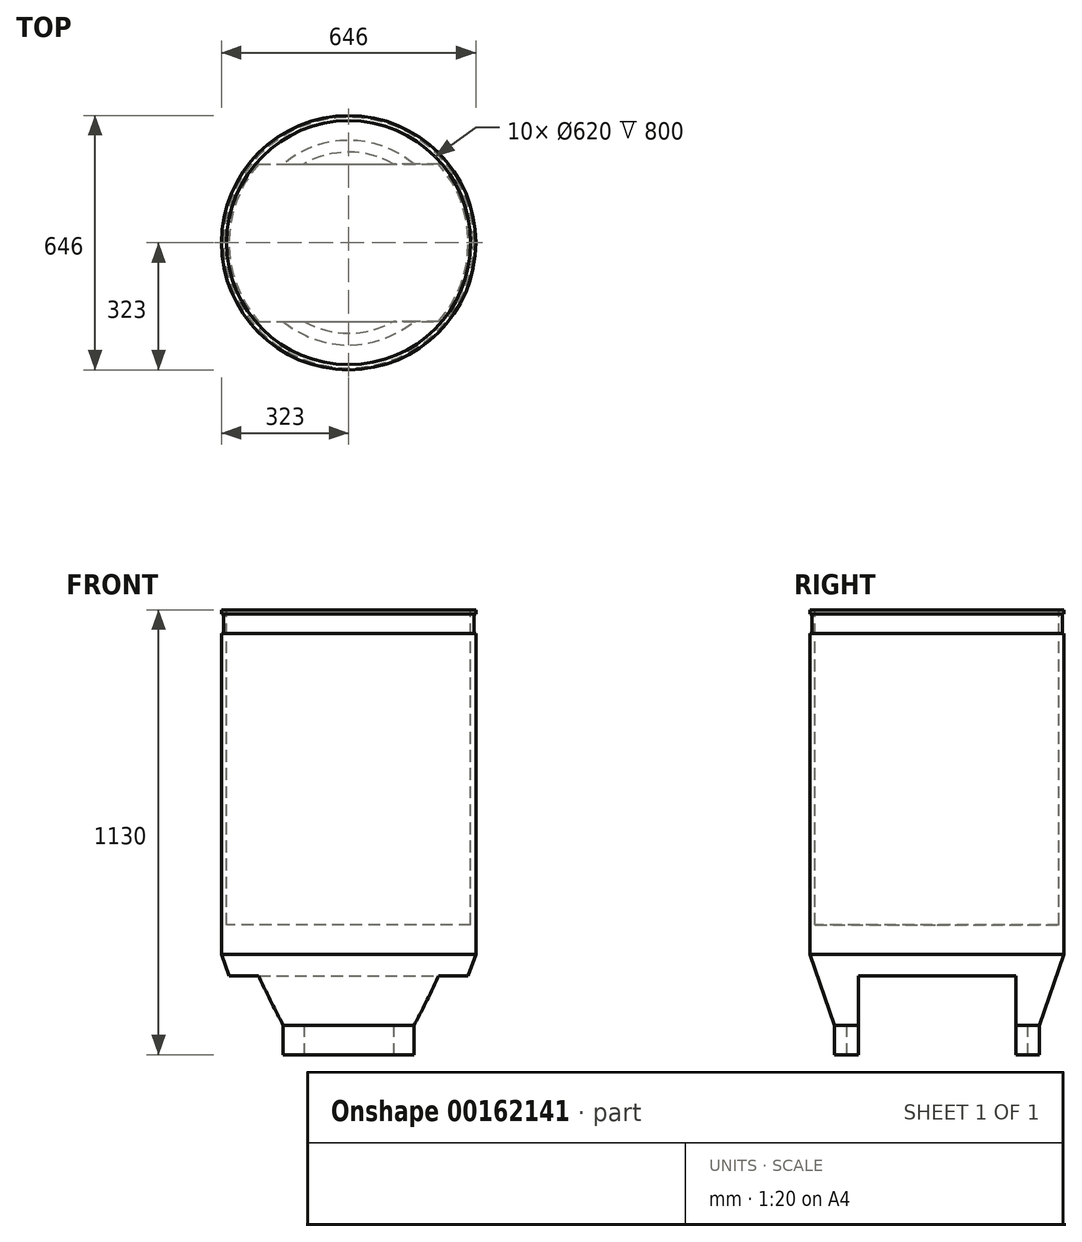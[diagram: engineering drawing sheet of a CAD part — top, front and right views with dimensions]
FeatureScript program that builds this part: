
annotation { "Feature Type Name" : "Feature", "Feature Type Description" : "" }
export const myFeature = defineFeature(function(context is Context, id is Id, definition is map)
    precondition{}
    {
        {
            var Q0;
            Q0=qCreatedBy(makeId("Front.planeOp"),FACE);
            var sketch = newSketch(context, id + "F0", { "sketchPlane" : qUnion([Q0])});
            skLineSegment(sketch, "E0", {"start": v(0, 0) * mm, "end": v(0, 1130) * mm});
            skLineSegment(sketch, "E1", {"start": v(0, 1130) * mm, "end": v(323, 1130) * mm});
            skLineSegment(sketch, "E2", {"start": v(323, 1130) * mm, "end": v(323, 1120) * mm});
            skLineSegment(sketch, "E3", {"start": v(323, 1120) * mm, "end": v(318, 1120) * mm});
            skLineSegment(sketch, "E4", {"start": v(318, 1120) * mm, "end": v(318, 1070) * mm});
            skLineSegment(sketch, "E5", {"start": v(318, 1070) * mm, "end": v(323, 1070) * mm});
            skLineSegment(sketch, "E6", {"start": v(323, 1070) * mm, "end": v(323, 255) * mm});
            skLineSegment(sketch, "E7", {"start": v(323, 255) * mm, "end": v(260, 75) * mm});
            skLineSegment(sketch, "E8", {"start": v(260, 75) * mm, "end": v(260, 0) * mm});
            skLineSegment(sketch, "E9", {"start": v(260, 0) * mm, "end": v(230, 0) * mm});
            skLineSegment(sketch, "E10", {"start": v(230, 0) * mm, "end": v(230, 75) * mm});
            skLineSegment(sketch, "E11", {"start": v(230, 75) * mm, "end": v(30, 75) * mm});
            skLineSegment(sketch, "E12", {"start": v(30, 75) * mm, "end": v(30, 0) * mm});
            skLineSegment(sketch, "E13", {"start": v(30, 0) * mm, "end": v(0, 0) * mm});
            skSolve(sketch);
        }
        {
            var Q0;
            Q0 = qSketchRegion(id + "F0", true);
            var Q1;
            Q1=sQuery(id+"F0.wireOp",EDGE,"E0");
            revolve(context, id + "F1", {"entities" : qUnion([Q0]), "axis" : qUnion([Q1]), "revolveType" : RevolveType.FULL});
        }
        {
            var Q0;
            Q0=makeQuery(id+"F1.opRevolve","SWEPT_FACE",FACE,{"disambiguationData":[OSD([sQuery(id+"F0.wireOp",EDGE,"E1")])]});
            var sketch = newSketch(context, id + "F2", { "sketchPlane" : qUnion([Q0])});
            skCircle(sketch, "E14", {"center": v(0, 0) * mm, "radius": 310 * mm});
            skSolve(sketch);
        }
        {
            var Q0;
            Q0 = qSketchRegion(id + "F2", true);
            extrude(context, id + "F3", {"entities" : qUnion([Q0]), "operationType" : NewBodyOperationType.REMOVE, "oppositeDirection" : true, "depth" : 800 * mm});
        }
        {
            var Q0;
            Q0=qCreatedBy(makeId("Right.planeOp"),FACE);
            var sketch = newSketch(context, id + "F4", { "sketchPlane" : qUnion([Q0])});
            skLineSegment(sketch, "E15.bottom", {"start": v(-200, 200) * mm, "end": v(200, 200) * mm});
            skLineSegment(sketch, "E15.top", {"start": v(-200, -50) * mm, "end": v(200, -50) * mm});
            skLineSegment(sketch, "E15.left", {"start": v(-200, 200) * mm, "end": v(-200, -50) * mm});
            skLineSegment(sketch, "E15.right", {"start": v(200, 200) * mm, "end": v(200, -50) * mm});
            skSolve(sketch);
        }
        {
            var Q0;
            Q0 = qSketchRegion(id + "F4", true);
            extrude(context, id + "F5", {"entities" : qUnion([Q0]), "operationType" : NewBodyOperationType.REMOVE, "endBound" : BoundingType.THROUGH_ALL, "oppositeDirection" : true, "depth" : 25 * mm});
        }
        {
            var Q0;
            Q0 = qSketchRegion(id + "F4", true);
            extrude(context, id + "F6", {"entities" : qUnion([Q0]), "operationType" : NewBodyOperationType.REMOVE, "endBound" : BoundingType.THROUGH_ALL, "depth" : 25 * mm});
        }
    });
